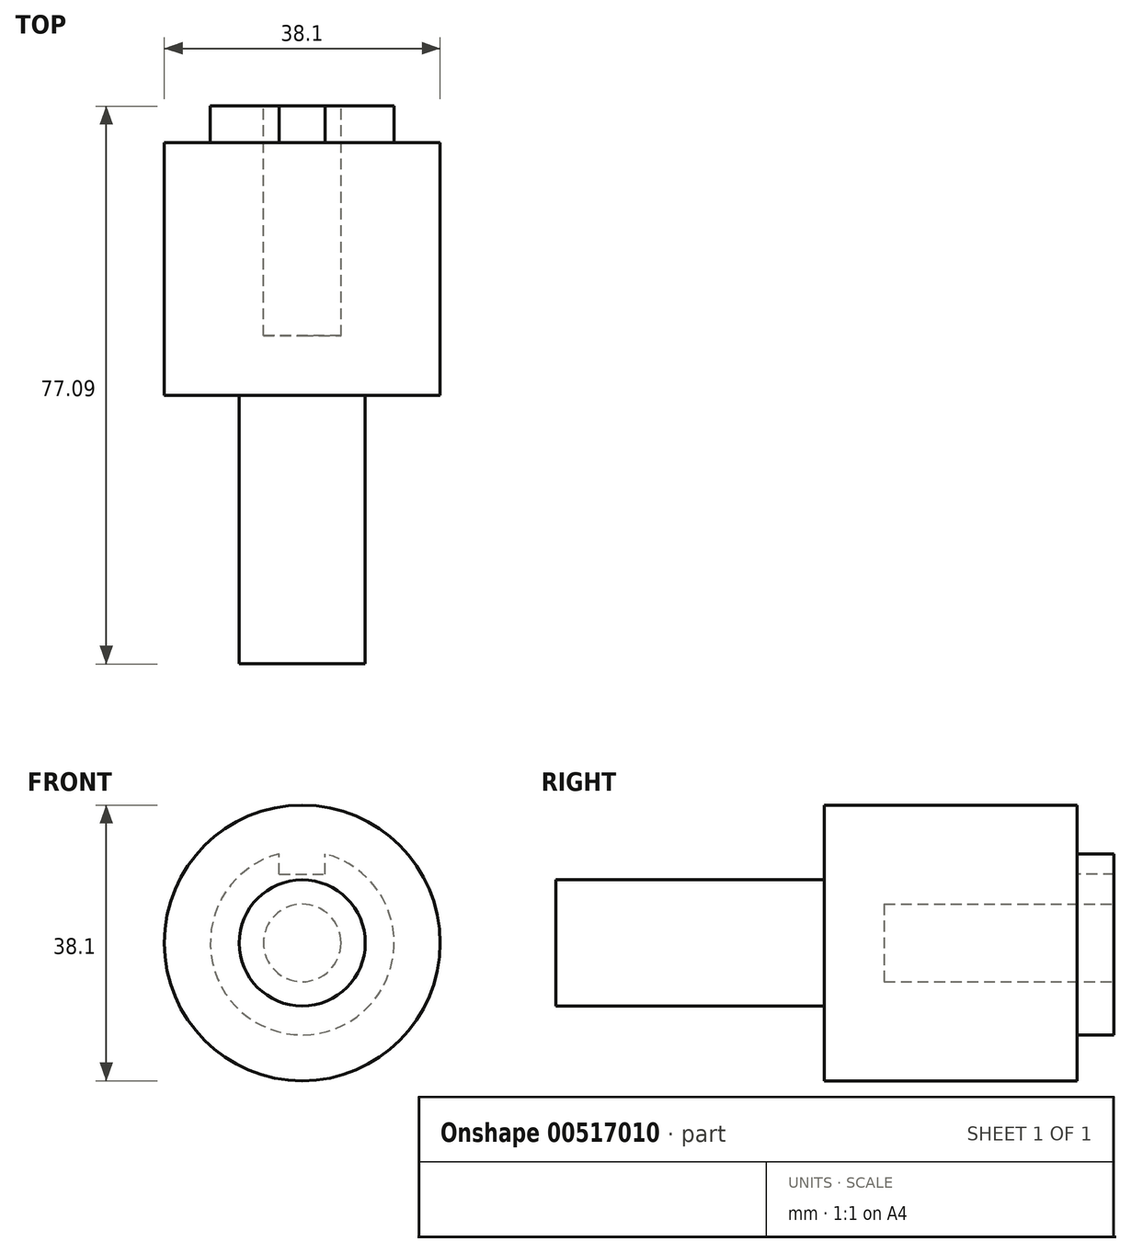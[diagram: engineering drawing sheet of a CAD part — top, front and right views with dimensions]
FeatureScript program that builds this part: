
annotation { "Feature Type Name" : "Feature", "Feature Type Description" : "" }
export const myFeature = defineFeature(function(context is Context, id is Id, definition is map)
    precondition{}
    {
        {
            var Q0;
            Q0=qCreatedBy(makeId("Front.planeOp"),FACE);
            var sketch = newSketch(context, id + "F0", { "sketchPlane" : qUnion([Q0])});
            skCircle(sketch, "E0", {"center": v(0, 0) * mm, "radius": 19.05 * mm});
            skSolve(sketch);
        }
        {
            var Q0;
            Q0=makeQuery(id+"F0.imprint","IMPRINT",FACE,{"disambiguationData":[TD([[makeQuery(id+"F0.imprint","IMPRINT",EDGE,{"derivedFrom":sQuery(id+"F0.wireOp",EDGE,"E0")}),1.0]])]});
            extrude(context, id + "F1", {"entities" : qUnion([Q0]), "endBound" : BoundingType.SYMMETRIC, "depth" : 34.92 * mm, "offsetDistance" : 25.4 * mm});
        }
        {
            var Q0;
            Q0=makeQuery(id+"F1.opExtrude","CAP_FACE",FACE,{"disambiguationData":[OSD([sQuery(id+"F0.wireOp",EDGE,"E0")])],"isStart":false});
            var sketch = newSketch(context, id + "F2", { "sketchPlane" : qUnion([Q0])});
            skCircle(sketch, "E1", {"center": v(0, 0) * mm, "radius": 8.71 * mm});
            skSolve(sketch);
        }
        {
            var Q0;
            Q0=makeQuery(id+"F2.imprint","IMPRINT",FACE,{"disambiguationData":[TD([[makeQuery(id+"F2.imprint","IMPRINT",EDGE,{"derivedFrom":sQuery(id+"F2.wireOp",EDGE,"E1")}),1.0]])]});
            extrude(context, id + "F3", {"entities" : qUnion([Q0]), "operationType" : NewBodyOperationType.ADD, "depth" : 37.08 * mm, "offsetDistance" : 25.4 * mm});
        }
        {
            var Q0;
            Q0=makeQuery(id+"F1.opExtrude","CAP_FACE",FACE,{"disambiguationData":[OSD([sQuery(id+"F0.wireOp",EDGE,"E0")])],"isStart":true});
            var sketch = newSketch(context, id + "F4", { "sketchPlane" : qUnion([Q0])});
            skCircle(sketch, "E2", {"center": v(0, 0) * mm, "radius": 12.7 * mm});
            skSolve(sketch);
        }
        {
            var Q0;
            Q0=makeQuery(id+"F4.imprint","IMPRINT",FACE,{"disambiguationData":[TD([[makeQuery(id+"F4.imprint","IMPRINT",EDGE,{"derivedFrom":sQuery(id+"F4.wireOp",EDGE,"E2")}),1.0]])]});
            extrude(context, id + "F5", {"entities" : qUnion([Q0]), "operationType" : NewBodyOperationType.ADD, "depth" : 5.08 * mm, "offsetDistance" : 25.4 * mm});
        }
        {
            var Q0;
            Q0=makeQuery(id+"F5.opExtrude","CAP_FACE",FACE,{"disambiguationData":[OSD([sQuery(id+"F4.wireOp",EDGE,"E2")])],"isStart":false});
            var sketch = newSketch(context, id + "F6", { "sketchPlane" : qUnion([Q0])});
            skCircle(sketch, "E3", {"center": v(0, 0) * mm, "radius": 5.36 * mm});
            skSolve(sketch);
        }
        {
            var Q0;
            Q0=makeQuery(id+"F6.imprint","IMPRINT",FACE,{"disambiguationData":[TD([[makeQuery(id+"F6.imprint","IMPRINT",EDGE,{"derivedFrom":sQuery(id+"F6.wireOp",EDGE,"E3")}),1.0]])]});
            extrude(context, id + "F7", {"entities" : qUnion([Q0]), "operationType" : NewBodyOperationType.REMOVE, "oppositeDirection" : true, "depth" : 31.75 * mm, "offsetDistance" : 25.4 * mm});
        }
        {
            var Q0;
            Q0=makeQuery(id+"F1.opExtrude","CAP_FACE",FACE,{"disambiguationData":[OSD([sQuery(id+"F0.wireOp",EDGE,"E0")])],"isStart":true});
            var sketch = newSketch(context, id + "F8", { "sketchPlane" : qUnion([Q0])});
            skPoint(sketch, "E4", {"position": v(0, 12.7) * mm});
            skSolve(sketch);
        }
        {
            var Q0;
            Q0=qCreatedBy(makeId("Top.planeOp"),FACE);
            var Q1;
            Q1=sQuery(id+"F8.wireOp",VERTEX,"E4");
            cPlane(context, id + "F9", {"entities" : qUnion([Q0, Q1]), "cplaneType" : CPlaneType.PLANE_POINT, "offset" : 25.4 * mm, "width" : 152.4 * mm, "height" : 152.4 * mm});
        }
        {
            var Q0;
            Q0=qCreatedBy(id+"F9.planeOp",FACE);
            var sketch = newSketch(context, id + "F10", { "sketchPlane" : qUnion([Q0])});
            skLineSegment(sketch, "E5.bottom", {"start": v(-3.18, 22.54) * mm, "end": v(3.17, 22.54) * mm});
            skLineSegment(sketch, "E5.top", {"start": v(-3.18, 17.46) * mm, "end": v(3.17, 17.46) * mm});
            skLineSegment(sketch, "E5.left", {"start": v(-3.18, 22.54) * mm, "end": v(-3.18, 17.46) * mm});
            skLineSegment(sketch, "E5.right", {"start": v(3.17, 22.54) * mm, "end": v(3.17, 17.46) * mm});
            skSolve(sketch);
        }
        {
            var Q0;
            Q0 = qSketchRegion(id + "F10", true);
            extrude(context, id + "F11", {"entities" : qUnion([Q0]), "operationType" : NewBodyOperationType.REMOVE, "oppositeDirection" : true, "depth" : 3.17 * mm, "offsetDistance" : 25.4 * mm});
        }
    });
